# Revit family: RPC Shrub
name_source: partatom
category: Planting
revit_build: Autodesk Revit Architecture 2012 (Build: 20110210_1515)
units: mm (PartAtom-declared; Revit-internal decimal feet)

## types (34) — shared parameters
Assembly Code = G2050500

## per-type parameters (varying)
| type | Height | Type Comments |
| Acacia  3'-6" | 3' - 6" | Acacia |
| Barberry 3'-4" | 3' - 4" | Barberry |
| Boxwood  2'-9" | 2' - 9" | Boxwood |
| Burning Bush 4'-6" | 4' - 6" | Burning Bush |
| Century 1'-10" | 1' - 10" | Century |
| Fan Palm 5'-6" | 5' - 6" | Fan Palm |
| Forsythia 8'-0" | 8' - 0" | Forsythia |
| Fountain Grass 3'-6" | 3' - 6" | Fountain Grass |
| Fountain Grass (2) 4'-6" | 4' - 6" | Fountain Grass |
| Fraser Photina 7'-0" | 7' - 0" | Fraser Photina |
| Golden Flame Spirea 2'-9" | 2' - 9" | Golden Flame Spirea |
| Holly 4'-3" | 4' - 3" | Holly |
| Holly (2) 4'-3" | 4' - 3" | Holly |
| Hydrangea 3'-9" | 3' - 9" | Hydrangea |
| Juniper 3'-0" | 3' - 0" | Juniper |
| Lilac 7'-6" | 7' - 6" | Lilac |
| Lupin 3'-10" | 3' - 10" | Lupin |
| Magnolia 3'-4" | 3' - 4" | Magnolia |
| Oleander 5'-4" | 5' - 4" | Oleander |
| Pampas Grass 8'-0" | 8' - 0" | Pampas Grass |
| Pearl Bush 6'-0" | 6' - 0" | Pearl Bush |
| Prairie Dropseed 5'-0" | 5' - 0" | Prairie Dropseed |
| Privet 3'-3" | 3' - 3" | Privet |
| Rhododendron 4'-0" | 4' - 0" | Rhododendron |
| Sweet Mock Orange 2'-0" | 2' - 0" | Sweet Mock Orange |
| Switchgrass 4'-6" | 4' - 6" | Switchgrass |
| Switchgrass (2) 4'-0" | 4' - 0" | Switchgrass |
| Thevetia 5'-6" | 5' - 6" | Thevetia |
| Vibernum 3'-0" | 3' - 0" | Vibernum |
| Yew 2'-4" | 2' - 4" | Yew |
| Cedar Shrub 3'-0" | 3' - 0" | Cedar Shrub |
| Daphne 3'-0" | 3' - 0" | Daphne |
| Hibiscus 5'-0" | 5' - 0" | Hibiscus Syriacus |
| Meadowlark 3'-0" | 3' - 0" | Meadowlark |

## geometry (parser evidence)
native form markers: Sweep x2
no freeform markers — native parametric forms only
